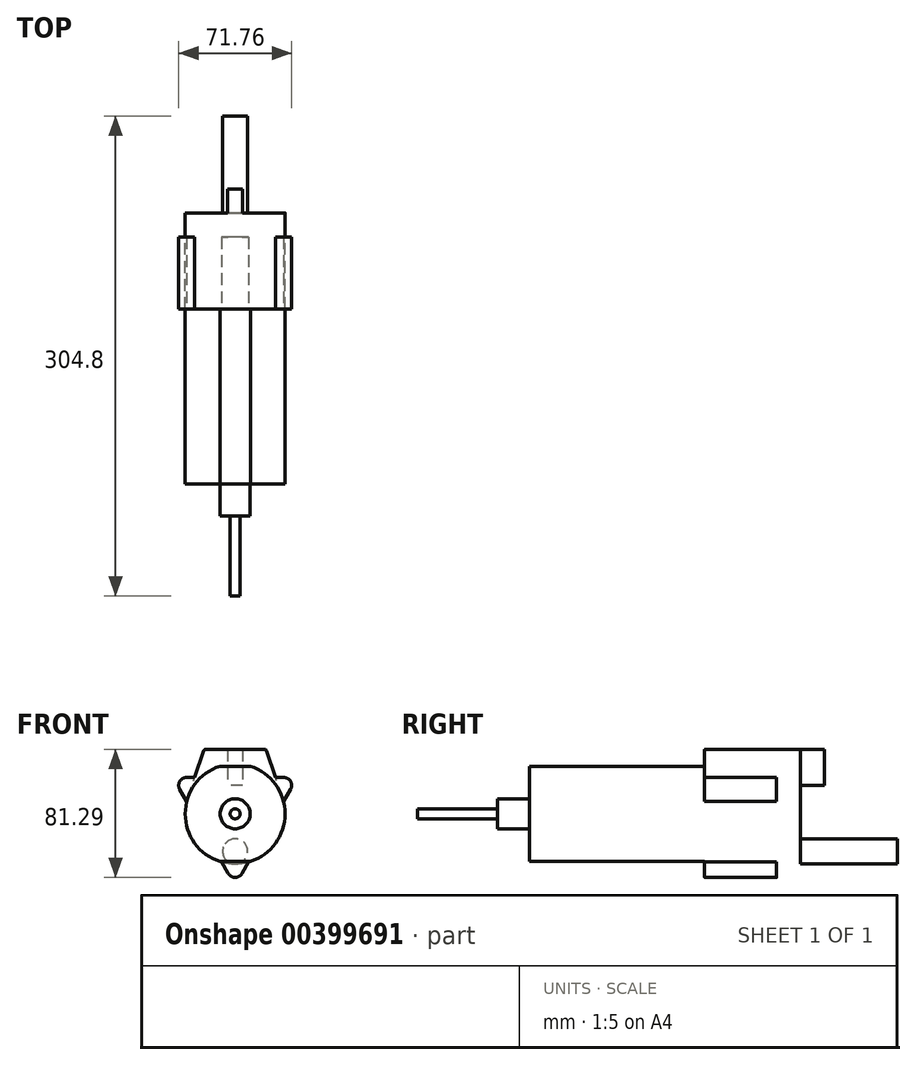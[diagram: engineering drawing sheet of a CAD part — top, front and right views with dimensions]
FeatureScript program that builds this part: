
annotation { "Feature Type Name" : "Feature", "Feature Type Description" : "" }
export const myFeature = defineFeature(function(context is Context, id is Id, definition is map)
    precondition{}
    {
        {
            var Q0;
            Q0=qCreatedBy(makeId("Front.planeOp"),FACE);
            var sketch = newSketch(context, id + "F0", { "sketchPlane" : qUnion([Q0])});
            skArc(sketch, "E0", {"start": v(-9.72, 30.23) * mm, "mid": v(-31.75, 0) * mm, "end": v(-9.72, -30.23) * mm});
            skLineSegment(sketch, "E1", {"start": v(-9.72, 30.23) * mm, "end": v(9.72, 30.23) * mm});
            skLineSegment(sketch, "E2", {"start": v(0, 0) * mm, "end": v(35.7, 0) * mm, "construction": true});
            skLineSegment(sketch, "E3.MirrorCS", {"start": v(-9.72, -30.23) * mm, "end": v(9.72, -30.23) * mm});
            skPoint(sketch, "E4.orphan", {"position": v(-23.22, 30.23) * mm});
            skPoint(sketch, "E5.orphan", {"position": v(22.28, 30.23) * mm});
            skPoint(sketch, "E6.orphan", {"position": v(22.28, -30.23) * mm});
            skPoint(sketch, "E7.orphan", {"position": v(-23.22, -30.23) * mm});
            skArc(sketch, "E8.trimOffspring", {"start": v(9.72, -30.23) * mm, "mid": v(31.75, 0) * mm, "end": v(9.72, 30.23) * mm});
            skSolve(sketch);
        }
        {
            var Q0;
            Q0=makeQuery(id+"F0.imprint","IMPRINT",FACE,{"disambiguationData":[TD([[makeQuery(id+"F0.imprint","IMPRINT",EDGE,{"derivedFrom":sQuery(id+"F0.wireOp",EDGE,"E0")}),1.0]])]});
            extrude(context, id + "F1", {"entities" : qUnion([Q0]), "endBound" : BoundingType.SYMMETRIC, "depth" : 111.12 * mm});
        }
        {
            var Q0;
            Q0=makeQuery(id+"F1.opExtrude","CAP_FACE",FACE,{"disambiguationData":[OSD([sQuery(id+"F0.wireOp",EDGE,"E0"),sQuery(id+"F0.wireOp",EDGE,"E1"),sQuery(id+"F0.wireOp",EDGE,"E3.MirrorCS"),sQuery(id+"F0.wireOp",EDGE,"E8.trimOffspring")])],"isStart":false});
            var sketch = newSketch(context, id + "F2", { "sketchPlane" : qUnion([Q0])});
            skCircle(sketch, "E9", {"center": v(0, 0) * mm, "radius": 9.53 * mm});
            skSolve(sketch);
        }
        {
            var Q0;
            Q0=makeQuery(id+"F2.imprint","IMPRINT",FACE,{"disambiguationData":[TD([[makeQuery(id+"F2.imprint","IMPRINT",EDGE,{"derivedFrom":sQuery(id+"F2.wireOp",EDGE,"E9")}),1.0]])]});
            extrude(context, id + "F3", {"entities" : qUnion([Q0]), "operationType" : NewBodyOperationType.ADD, "depth" : 20.32 * mm});
        }
        {
            var Q0;
            Q0=makeQuery(id+"F1.opExtrude","CAP_FACE",FACE,{"disambiguationData":[OSD([sQuery(id+"F0.wireOp",EDGE,"E0"),sQuery(id+"F0.wireOp",EDGE,"E1"),sQuery(id+"F0.wireOp",EDGE,"E3.MirrorCS"),sQuery(id+"F0.wireOp",EDGE,"E8.trimOffspring")])],"isStart":true});
            var sketch = newSketch(context, id + "F4", { "sketchPlane" : qUnion([Q0])});
            skLineSegment(sketch, "E10", {"start": v(-30.8, 23.12) * mm, "end": v(30.8, 23.12) * mm});
            skLineSegment(sketch, "E11", {"start": v(35.2, 15.5) * mm, "end": v(4.4, -37.85) * mm});
            skLineSegment(sketch, "E12", {"start": v(-4.4, -37.85) * mm, "end": v(-35.2, 15.5) * mm});
            skPoint(sketch, "E13.visualSharp", {"position": v(39.6, 23.12) * mm});
            skArc(sketch, "E13.filletArc", {"start": v(35.2, 15.5) * mm, "mid": v(35.2, 20.58) * mm, "end": v(30.8, 23.12) * mm});
            skPoint(sketch, "E14.visualSharp", {"position": v(-39.6, 23.12) * mm});
            skArc(sketch, "E14.filletArc", {"start": v(-30.8, 23.12) * mm, "mid": v(-35.2, 20.58) * mm, "end": v(-35.2, 15.5) * mm});
            skPoint(sketch, "E15.visualSharp", {"position": v(0, -45.47) * mm});
            skArc(sketch, "E15.filletArc", {"start": v(-4.4, -37.85) * mm, "mid": v(0, -40.39) * mm, "end": v(4.4, -37.85) * mm});
            skSolve(sketch);
        }
        {
            var Q0;
            {var subQ0=sQuery(id+"F4.wireOp",EDGE,"E10");var subQ9=makeQuery(id+"F1.opExtrude","CAP_EDGE",EDGE,{"disambiguationData":[OSD([sQuery(id+"F0.wireOp",EDGE,"E8.trimOffspring")])],"isStart":true});var subQ11=makeQuery(id+"F4.imprint","INTERSECT",VERTEX,{"derivedFrom":[subQ9,subQ0]});Q0=makeQuery(id+"F4.imprint","IMPRINT",FACE,{"disambiguationData":[TD([[makeQuery(id+"F4.imprint","IMPRINT",EDGE,{"disambiguationData":[TD([[subQ11,-1.0]])],"derivedFrom":subQ0}),-1.0]])]});}
            var Q1;
            {var subQ0=sQuery(id+"F4.wireOp",EDGE,"E14.filletArc");Q1=makeQuery(id+"F4.imprint","IMPRINT",FACE,{"disambiguationData":[TD([[makeQuery(id+"F4.imprint","IMPRINT",EDGE,{"derivedFrom":subQ0}),1.0]])]});}
            var Q2;
            {var subQ0=sQuery(id+"F4.wireOp",EDGE,"E15.filletArc");Q2=makeQuery(id+"F4.imprint","IMPRINT",FACE,{"disambiguationData":[TD([[makeQuery(id+"F4.imprint","IMPRINT",EDGE,{"derivedFrom":subQ0}),1.0]])]});}
            var Q3;
            {var subQ0=sQuery(id+"F4.wireOp",EDGE,"E13.filletArc");Q3=makeQuery(id+"F4.imprint","IMPRINT",FACE,{"disambiguationData":[TD([[makeQuery(id+"F4.imprint","IMPRINT",EDGE,{"derivedFrom":subQ0}),1.0]])]});}
            extrude(context, id + "F5", {"entities" : qUnion([Q0, Q1, Q2, Q3]), "operationType" : NewBodyOperationType.ADD, "depth" : 45.72 * mm});
        }
        {
            var Q0;
            {var subQ1=sQuery(id+"F0.wireOp",EDGE,"E1");var subQ2=sQuery(id+"F0.wireOp",EDGE,"E8.trimOffspring");var subQ3=sQuery(id+"F0.wireOp",EDGE,"E0");Q0=makeQuery(id+"F5.boolean.opBoolean","SPLIT",FACE,{"disambiguationData":[TD([makeQuery(id+"F1.opExtrude","SWEPT_FACE",FACE,{"disambiguationData":[OSD([subQ1])]})])],"derivedFrom":makeQuery(id+"F1.opExtrude","CAP_FACE",FACE,{"disambiguationData":[OSD([subQ3,subQ1,sQuery(id+"F0.wireOp",EDGE,"E3.MirrorCS"),subQ2])],"isStart":true})});}
            var sketch = newSketch(context, id + "F6", { "sketchPlane" : qUnion([Q0])});
            skArc(sketch, "E16.0", {"start": v(9.72, 30.23) * mm, "mid": v(16.14, 27.34) * mm, "end": v(21.76, 23.12) * mm, "construction": true});
            skCircle(sketch, "E17", {"center": v(0, 0) * mm, "radius": 31.75 * mm});
            skSolve(sketch);
        }
        {
            var Q0;
            {var subQ1=sQuery(id+"F0.wireOp",EDGE,"E1");var subQ2=makeQuery(id+"F1.opExtrude","CAP_EDGE",EDGE,{"disambiguationData":[OSD([subQ1])],"isStart":true});Q0=makeQuery(id+"F6.imprint","IMPRINT",FACE,{"disambiguationData":[TD([[makeQuery(id+"F6.imprint","IMPRINT",EDGE,{"derivedFrom":subQ2}),1.0]])]});}
            var Q1;
            {var subQ1=sQuery(id+"F4.wireOp",EDGE,"E10");var subQ2=makeQuery(id+"F5.boolean.opBoolean","SPLIT",EDGE,{"disambiguationData":[topologyDisambiguationEdgeConnected([makeQuery(id+"F1.opExtrude","CAP_FACE",FACE,{"disambiguationData":[OSD([sQuery(id+"F0.wireOp",EDGE,"E0"),sQuery(id+"F0.wireOp",EDGE,"E1"),sQuery(id+"F0.wireOp",EDGE,"E3.MirrorCS"),sQuery(id+"F0.wireOp",EDGE,"E8.trimOffspring")])],"isStart":true}),makeQuery(id+"F5.opExtrude","SWEPT_FACE",FACE,{"disambiguationData":[OSD([subQ1])]})])],"derivedFrom":makeQuery(id+"F5.opExtrude","CAP_EDGE",EDGE,{"disambiguationData":[OSD([subQ1])],"isStart":true})});Q1=makeQuery(id+"F6.imprint","IMPRINT",FACE,{"disambiguationData":[TD([[makeQuery(id+"F6.imprint","IMPRINT",EDGE,{"derivedFrom":subQ2}),-1.0]])]});}
            var Q2;
            {var subQ1=makeQuery(id+"F1.opExtrude","CAP_EDGE",EDGE,{"disambiguationData":[OSD([sQuery(id+"F0.wireOp",EDGE,"E1")])],"isStart":true});Q2=makeQuery(id+"F6.imprint","IMPRINT",FACE,{"disambiguationData":[TD([[makeQuery(id+"F6.imprint","IMPRINT",EDGE,{"derivedFrom":subQ1}),-1.0]])]});}
            extrude(context, id + "F7", {"entities" : qUnion([Q0, Q1, Q2]), "operationType" : NewBodyOperationType.ADD, "depth" : 60.96 * mm});
        }
        {
            var Q0;
            Q0=makeQuery(id+"F7.opExtrude","CAP_FACE",FACE,{"disambiguationData":[OSD([sQuery(id+"F6.wireOp",EDGE,"E17")])],"isStart":false});
            var sketch = newSketch(context, id + "F8", { "sketchPlane" : qUnion([Q0])});
            skCircle(sketch, "E18.0", {"center": v(0, 0) * mm, "radius": 31.75 * mm, "construction": true});
            skLineSegment(sketch, "E19", {"start": v(-29.3, 40.9) * mm, "end": v(29.3, 40.9) * mm});
            skLineSegment(sketch, "E20", {"start": v(30.08, 10.15) * mm, "end": v(19.7, 40.9) * mm});
            skLineSegment(sketch, "E21", {"start": v(-30.08, 10.15) * mm, "end": v(-19.7, 40.9) * mm});
            skLineSegment(sketch, "E22", {"start": v(0, 0) * mm, "end": v(0, 48.07) * mm, "construction": true});
            skPoint(sketch, "E22.endSnap0", {"position": v(0, 40.9) * mm});
            skLineSegment(sketch, "E23.0", {"start": v(21.76, 23.12) * mm, "end": v(30.8, 23.12) * mm, "construction": true});
            skSolve(sketch);
        }
        {
            var Q0;
            {var subQ0=sQuery(id+"F8.wireOp",EDGE,"E20");Q0=makeQuery(id+"F8.imprint","IMPRINT",FACE,{"disambiguationData":[TD([[makeQuery(id+"F8.imprint","IMPRINT",EDGE,{"derivedFrom":subQ0}),1.0]])]});}
            extrude(context, id + "F9", {"entities" : qUnion([Q0]), "operationType" : NewBodyOperationType.ADD, "oppositeDirection" : true, "depth" : 60.96 * mm});
        }
        {
            var Q0;
            Q0=makeQuery(id+"F9.opExtrude","SWEPT_EDGE",EDGE,{"disambiguationData":[OSD([sQuery(id+"F8.wireOp",EDGE,"E19"),sQuery(id+"F8.wireOp",EDGE,"E21")])]});
            var Q1;
            Q1=makeQuery(id+"F9.opExtrude","SWEPT_EDGE",EDGE,{"disambiguationData":[OSD([sQuery(id+"F8.wireOp",EDGE,"E19"),sQuery(id+"F8.wireOp",EDGE,"E20")])]});
            fillet(context, id + "F10", {"entities" : qUnion([Q0, Q1]), "radius" : 1.27 * mm, "tangentPropagation" : true, "allowEdgeOverflow" : false});
        }
        {
            var Q0;
            {var subQ0=sQuery(id+"F6.wireOp",EDGE,"E17");Q0=makeQuery(id+"F9.boolean.opBoolean","MERGE",FACE,{"derivedFrom":[makeQuery(id+"F7.opExtrude","CAP_FACE",FACE,{"disambiguationData":[OSD([subQ0])],"isStart":false}),makeQuery(id+"F9.opExtrude","CAP_FACE",FACE,{"disambiguationData":[OSD([subQ0,sQuery(id+"F8.wireOp",EDGE,"E19"),sQuery(id+"F8.wireOp",EDGE,"E20"),sQuery(id+"F8.wireOp",EDGE,"E21")])],"isStart":true})]});}
            var sketch = newSketch(context, id + "F11", { "sketchPlane" : qUnion([Q0])});
            skLineSegment(sketch, "E24.0", {"start": v(-18.8, 40.9) * mm, "end": v(18.8, 40.9) * mm, "construction": true});
            skLineSegment(sketch, "E25.bottom", {"start": v(-4.76, 40.9) * mm, "end": v(4.76, 40.9) * mm});
            skLineSegment(sketch, "E25.top", {"start": v(-4.76, 18.04) * mm, "end": v(4.76, 18.04) * mm});
            skLineSegment(sketch, "E25.left", {"start": v(-4.76, 40.9) * mm, "end": v(-4.76, 18.04) * mm});
            skLineSegment(sketch, "E25.right", {"start": v(4.76, 40.9) * mm, "end": v(4.76, 18.04) * mm});
            skSolve(sketch);
        }
        {
            var Q0;
            Q0=makeQuery(id+"F11.imprint","IMPRINT",FACE,{"disambiguationData":[TD([[makeQuery(id+"F11.imprint","IMPRINT",EDGE,{"derivedFrom":sQuery(id+"F11.wireOp",EDGE,"E25.bottom")}),-1.0]])]});
            extrude(context, id + "F12", {"entities" : qUnion([Q0]), "operationType" : NewBodyOperationType.ADD, "depth" : 15.24 * mm});
        }
        {
            var Q0;
            {var subQ0=sQuery(id+"F6.wireOp",EDGE,"E17");Q0=makeQuery(id+"F9.boolean.opBoolean","MERGE",FACE,{"derivedFrom":[makeQuery(id+"F7.opExtrude","CAP_FACE",FACE,{"disambiguationData":[OSD([subQ0])],"isStart":false}),makeQuery(id+"F9.opExtrude","CAP_FACE",FACE,{"disambiguationData":[OSD([subQ0,sQuery(id+"F8.wireOp",EDGE,"E19"),sQuery(id+"F8.wireOp",EDGE,"E20"),sQuery(id+"F8.wireOp",EDGE,"E21")])],"isStart":true})]});}
            var sketch = newSketch(context, id + "F13", { "sketchPlane" : qUnion([Q0])});
            skLineSegment(sketch, "E26", {"start": v(0, 0) * mm, "end": v(0, -36.23) * mm, "construction": true});
            skCircle(sketch, "E27", {"center": v(0, -23.81) * mm, "radius": 7.94 * mm});
            skSolve(sketch);
        }
        {
            var Q0;
            Q0=makeQuery(id+"F13.imprint","IMPRINT",FACE,{"disambiguationData":[TD([[makeQuery(id+"F13.imprint","IMPRINT",EDGE,{"derivedFrom":sQuery(id+"F13.wireOp",EDGE,"E27")}),1.0]])]});
            extrude(context, id + "F14", {"entities" : qUnion([Q0]), "operationType" : NewBodyOperationType.ADD, "depth" : 61.6 * mm});
        }
        {
            var Q0;
            Q0=makeQuery(id+"F3.opExtrude","CAP_FACE",FACE,{"disambiguationData":[OSD([sQuery(id+"F2.wireOp",EDGE,"E9")])],"isStart":false});
            var sketch = newSketch(context, id + "F15", { "sketchPlane" : qUnion([Q0])});
            skCircle(sketch, "E28", {"center": v(0, 0) * mm, "radius": 3.18 * mm});
            skSolve(sketch);
        }
        {
            var Q0;
            Q0=makeQuery(id+"F15.imprint","IMPRINT",FACE,{"disambiguationData":[TD([[makeQuery(id+"F15.imprint","IMPRINT",EDGE,{"derivedFrom":sQuery(id+"F15.wireOp",EDGE,"E28")}),1.0]])]});
            extrude(context, id + "F16", {"entities" : qUnion([Q0]), "depth" : 50.8 * mm});
        }
    });
